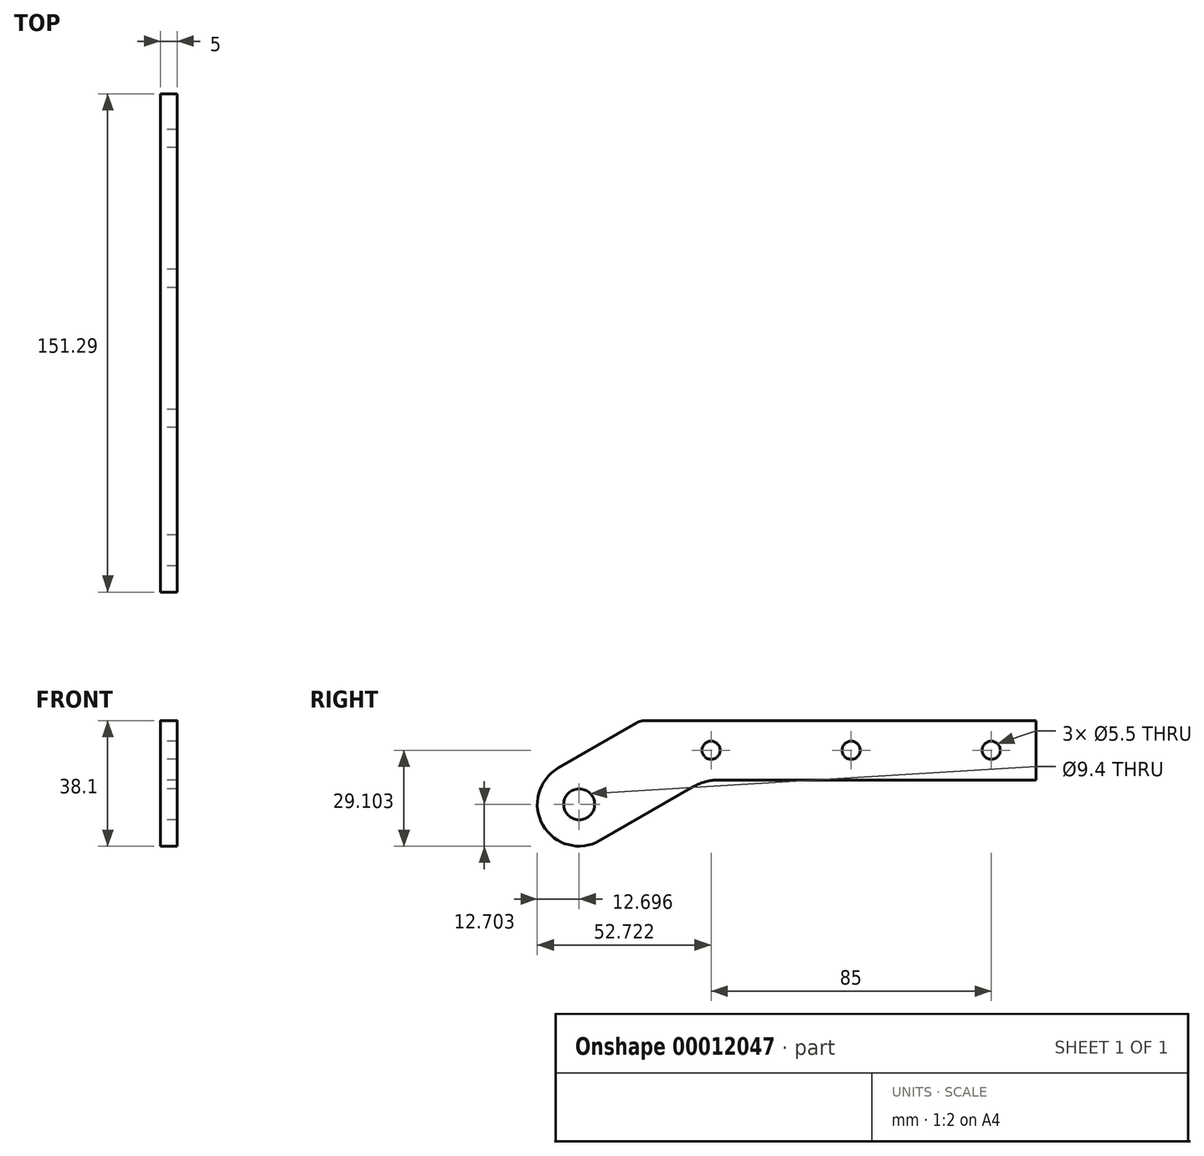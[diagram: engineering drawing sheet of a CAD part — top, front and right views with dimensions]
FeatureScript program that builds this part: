
annotation { "Feature Type Name" : "Feature", "Feature Type Description" : "" }
export const myFeature = defineFeature(function(context is Context, id is Id, definition is map)
    precondition{}
    {
        {
            var Q0;
            Q0=qCreatedBy(makeId("Right.planeOp"),FACE);
            var sketch = newSketch(context, id + "F0", { "sketchPlane" : qUnion([Q0])});
            skCircle(sketch, "E0", {"center": v(0.06, 0.1) * mm, "radius": 4.7 * mm});
            skArc(sketch, "E1", {"start": v(-6.3, 11.1) * mm, "mid": v(-10.94, -6.26) * mm, "end": v(6.4, -10.9) * mm});
            skLineSegment(sketch, "E2", {"start": v(19.99, 25.5) * mm, "end": v(138.65, 25.5) * mm});
            skLineSegment(sketch, "E3", {"start": v(-6.3, 11.1) * mm, "end": v(17.49, 24.82) * mm});
            skLineSegment(sketch, "E4", {"start": v(6.4, -10.9) * mm, "end": v(34.8, 5.48) * mm});
            skLineSegment(sketch, "E5.0", {"start": v(42.3, 7.5) * mm, "end": v(138.65, 7.5) * mm});
            skLineSegment(sketch, "E6", {"start": v(138.65, 25.5) * mm, "end": v(138.65, 7.5) * mm});
            skPoint(sketch, "E7.visualSharp", {"position": v(18.65, 25.5) * mm});
            skArc(sketch, "E7.filletArc", {"start": v(19.99, 25.5) * mm, "mid": v(18.7, 25.32) * mm, "end": v(17.49, 24.82) * mm});
            skPoint(sketch, "E8.visualSharp", {"position": v(38.27, 7.5) * mm});
            skArc(sketch, "E8.filletArc", {"start": v(42.3, 7.5) * mm, "mid": v(38.4, 6.98) * mm, "end": v(34.8, 5.48) * mm});
            skCircle(sketch, "E9", {"center": v(125.08, 16.5) * mm, "radius": 2.75 * mm});
            skCircle(sketch, "E10", {"center": v(82.58, 16.5) * mm, "radius": 2.75 * mm});
            skCircle(sketch, "E11", {"center": v(40.08, 16.5) * mm, "radius": 2.75 * mm});
            skSolve(sketch);
        }
        {
            var Q0;
            Q0=makeQuery(id+"F0.imprint","IMPRINT",FACE,{"disambiguationData":[TD([[makeQuery(id+"F0.imprint","IMPRINT",EDGE,{"derivedFrom":sQuery(id+"F0.wireOp",EDGE,"E0")}),-1.0]])]});
            extrude(context, id + "F1", {"entities" : qUnion([Q0]), "depth" : 5 * mm});
        }
    });
